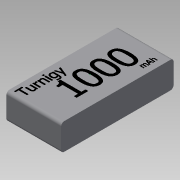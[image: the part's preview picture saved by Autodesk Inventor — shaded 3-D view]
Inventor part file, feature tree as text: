
AUTODESK INVENTOR PART (.ipt)
format: ipt  version: 2015 SP1 (Build 190203100, 203)  size: 85,504 bytes
history: native  units: mm
features: sketch x2, extrude x1, fillet x1
ambient origin geometry x8: Origin, YZ Plane, XZ Plane, XY Plane, X Axis, Y Axis, Z Axis, Center Point
bodies: Solid1 (feature_tree)
feature tree (4):
  extrude  "Extrusion1"  Depth=72.0mm
  fillet  "Fillet1"  Radius=17.0mm
  sketch  "Sketch3"  dims[d4=2.0mm]
  sketch  "Sketch1"  dims[d0=35.0mm d1=72.0mm d2=17.0mm d3=0.0mm]
